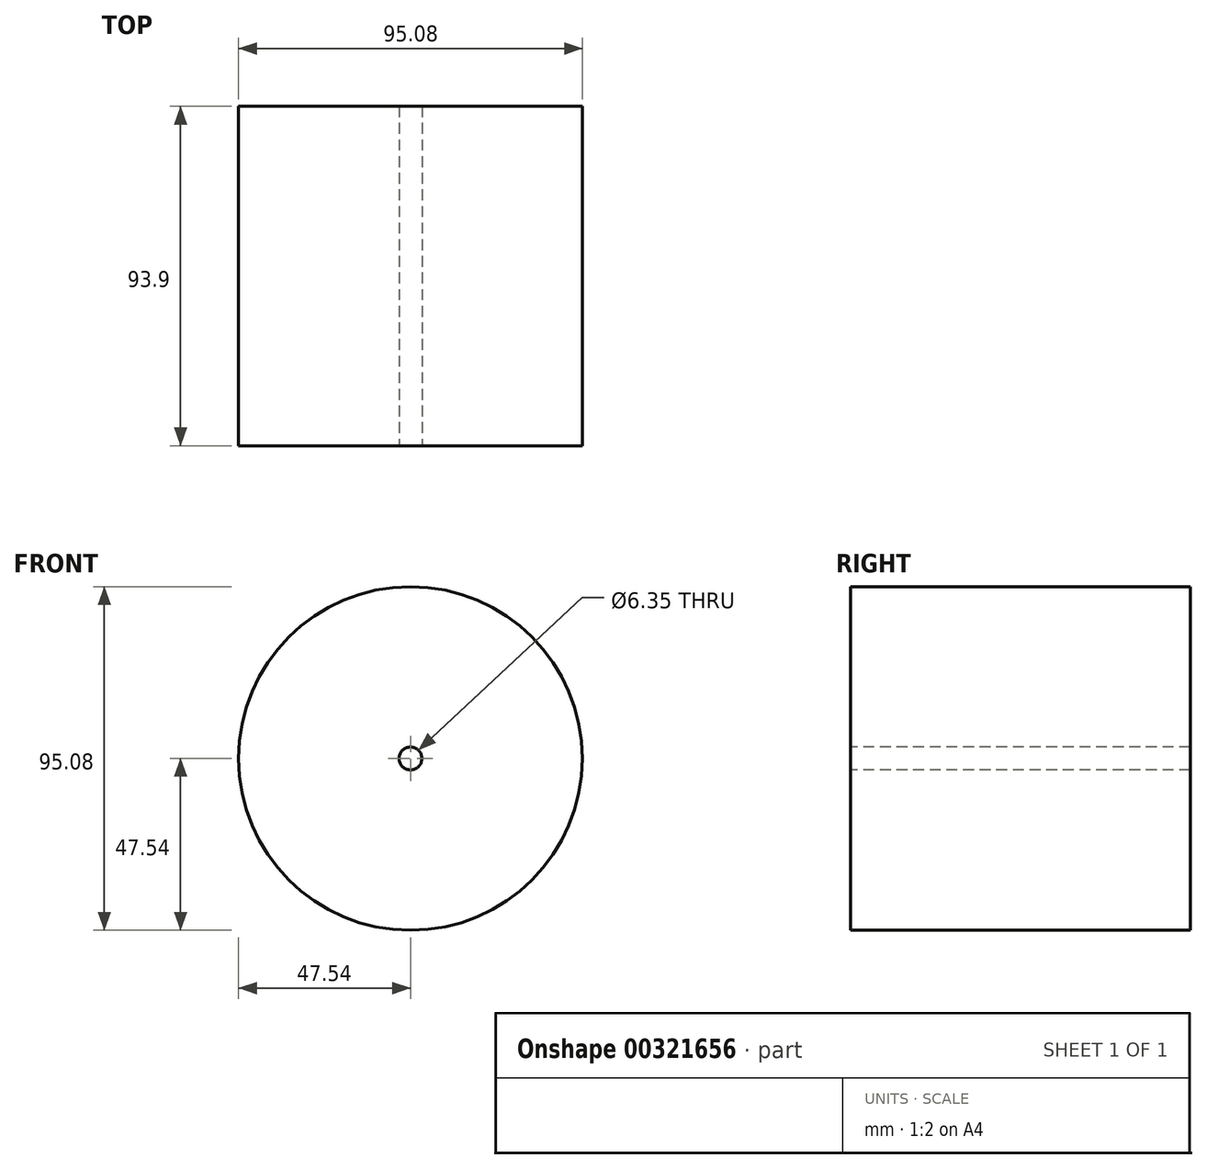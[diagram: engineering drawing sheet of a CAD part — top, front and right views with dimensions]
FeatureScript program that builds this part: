
annotation { "Feature Type Name" : "Feature", "Feature Type Description" : "" }
export const myFeature = defineFeature(function(context is Context, id is Id, definition is map)
    precondition{}
    {
        {
            var Q0;
            Q0=qCreatedBy(makeId("Front.planeOp"),FACE);
            var sketch = newSketch(context, id + "F0", { "sketchPlane" : qUnion([Q0])});
            skCircle(sketch, "E0", {"center": v(0, 0) * mm, "radius": 47.54 * mm});
            skSolve(sketch);
        }
        {
            var Q0;
            Q0 = qSketchRegion(id + "F0", true);
            extrude(context, id + "F1", {"entities" : qUnion([Q0]), "depth" : 93.9 * mm});
        }
        {
            var Q0;
            Q0=makeQuery(id+"F1.opExtrude","CAP_FACE",FACE,{"disambiguationData":[OSD([sQuery(id+"F0.wireOp",EDGE,"E0")])],"isStart":false});
            var sketch = newSketch(context, id + "F2", { "sketchPlane" : qUnion([Q0])});
            skCircle(sketch, "E1", {"center": v(0, 0) * mm, "radius": 38.74 * mm});
            skSolve(sketch);
        }
        {
            var Q0;
            Q0=sQuery(id+"F2.wireOp",VERTEX,"E1.center");
            var Q1;
            Q1=makeQuery(id+"F1.opExtrude","SWEPT_BODY",BODY,{"disambiguationData":[OSD([sQuery(id+"F0.wireOp",EDGE,"E0")])]});
            hole(context, id + "F3", {"style" : HoleStyle.SIMPLE, "endStyle" : HoleEndStyle.THROUGH, "holeDiameter" : 6.35 * mm, "tappedDepth" : 12.7 * mm, "tapClearance" : 3, "locations" : qUnion([Q0]), "scope" : qUnion([Q1])});
        }
    });
